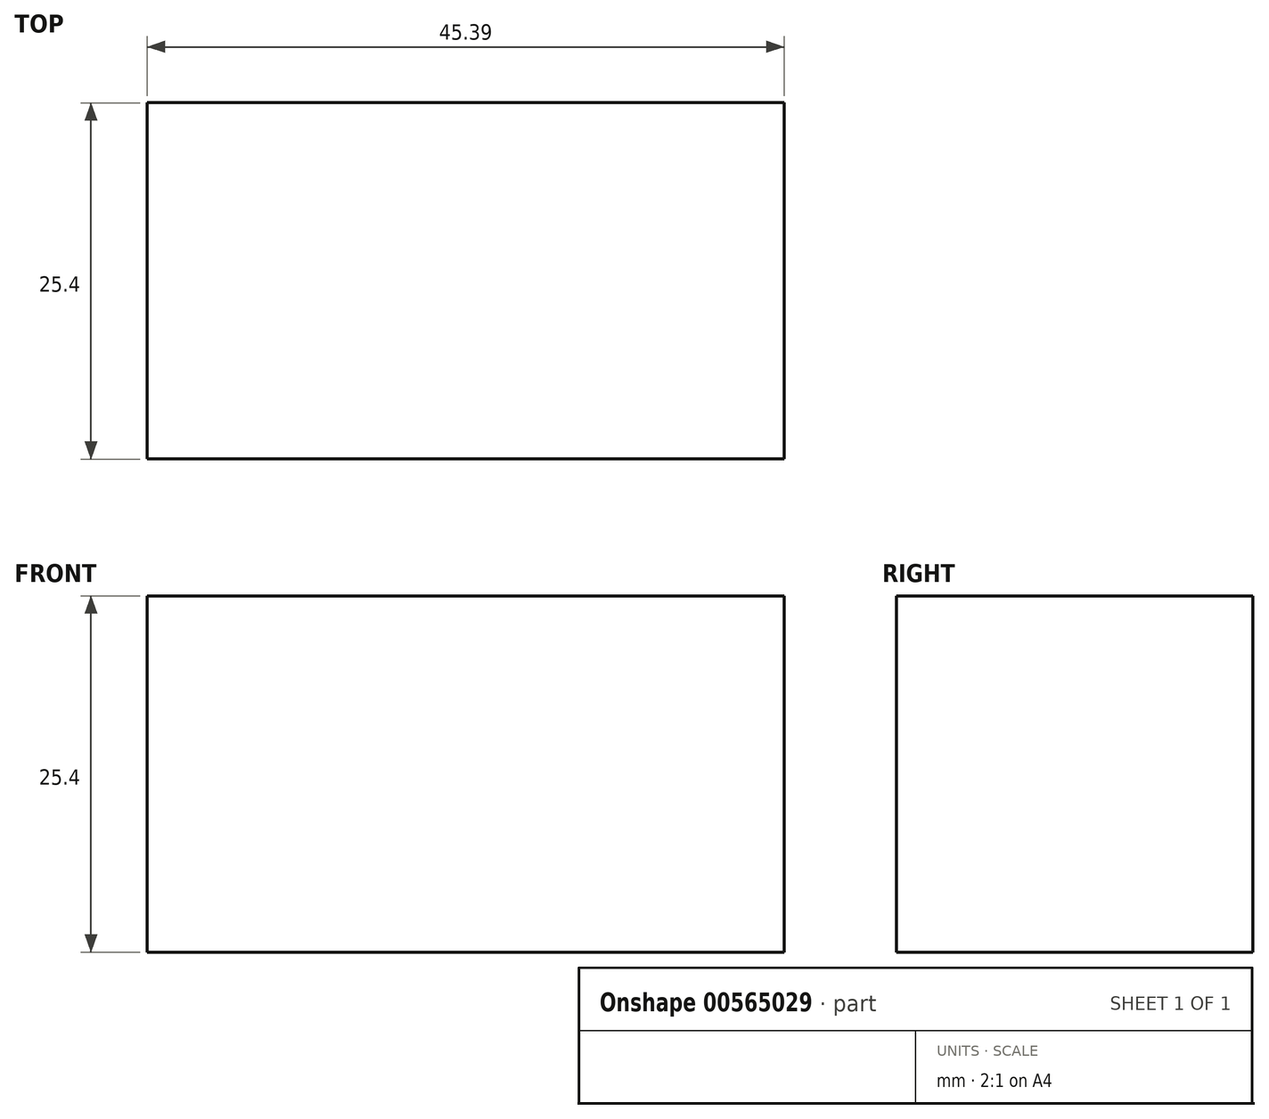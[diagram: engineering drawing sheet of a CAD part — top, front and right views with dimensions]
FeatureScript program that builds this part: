
annotation { "Feature Type Name" : "Feature", "Feature Type Description" : "" }
export const myFeature = defineFeature(function(context is Context, id is Id, definition is map)
    precondition{}
    {
        {
            var Q0;
            Q0=qCreatedBy(makeId("Top.planeOp"),FACE);
            var sketch = newSketch(context, id + "F0", { "sketchPlane" : qUnion([Q0])});
            skLineSegment(sketch, "E0.bottom", {"start": v(0, 0) * mm, "end": v(-45.4, 0) * mm});
            skLineSegment(sketch, "E0.top", {"start": v(0, 35.11) * mm, "end": v(-45.4, 35.11) * mm});
            skLineSegment(sketch, "E0.left", {"start": v(0, 0) * mm, "end": v(0, 35.11) * mm});
            skLineSegment(sketch, "E0.right", {"start": v(-45.4, 0) * mm, "end": v(-45.4, 35.11) * mm});
            skSolve(sketch);
        }
        {
            var Q0;
            Q0=sQuery(id+"F0.wireOp",EDGE,"E0.top");
            extrude(context, id + "F1", {"bodyType" : ToolBodyType.SURFACE, "surfaceEntities" : qUnion([Q0]), "depth" : 25.4 * mm, "offsetDistance" : 25.4 * mm});
        }
        {
            var Q0;
            Q0=makeQuery(id+"F1.opExtrude","SWEPT_FACE",FACE,{"disambiguationData":[OSD([sQuery(id+"F0.wireOp",EDGE,"E0.top")])]});
            extrude(context, id + "F2", {"entities" : qUnion([Q0]), "depth" : 25.4 * mm, "offsetDistance" : 25.4 * mm});
        }
    });
